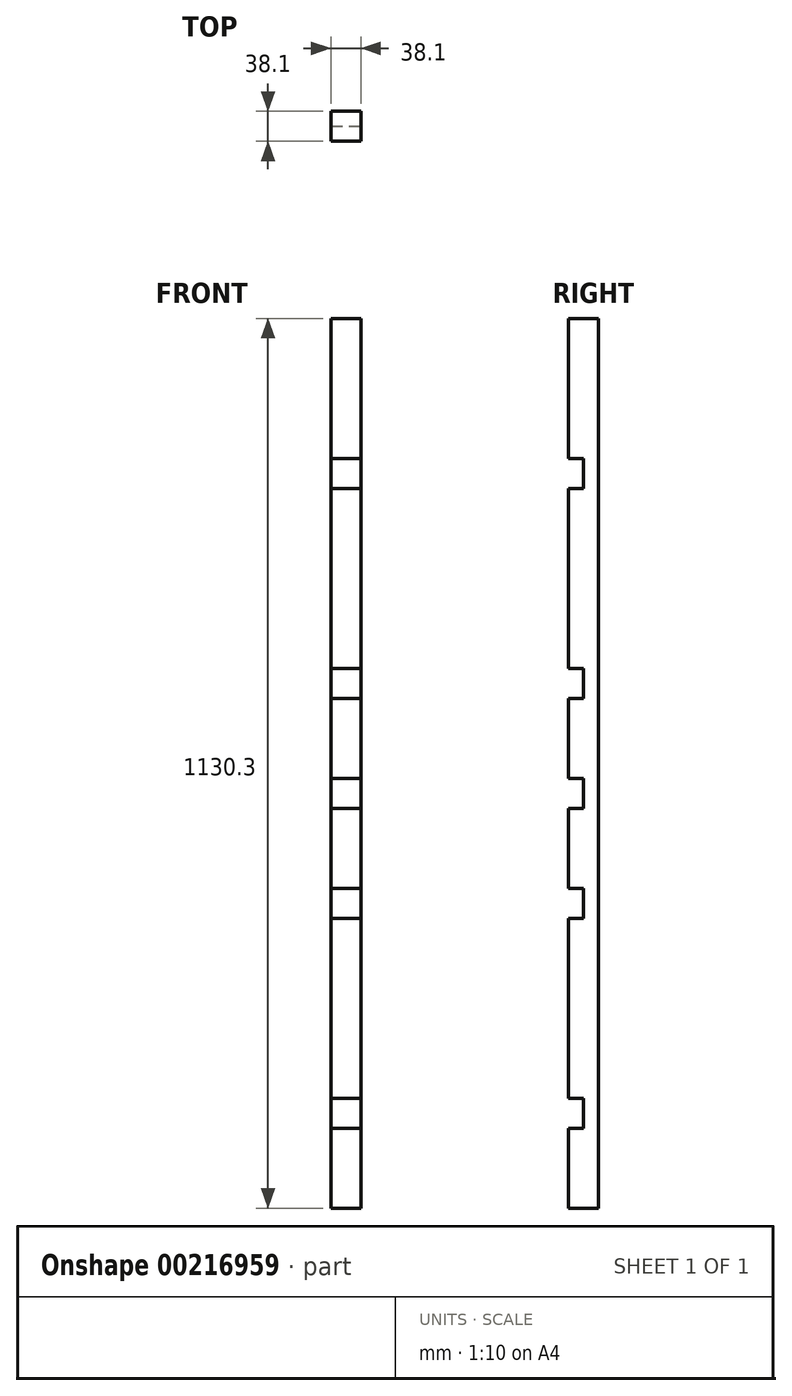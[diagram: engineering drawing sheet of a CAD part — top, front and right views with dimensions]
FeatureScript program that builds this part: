
annotation { "Feature Type Name" : "Feature", "Feature Type Description" : "" }
export const myFeature = defineFeature(function(context is Context, id is Id, definition is map)
    precondition{}
    {
        {
            var Q0;
            Q0=qCreatedBy(makeId("Top.planeOp"),FACE);
            var sketch = newSketch(context, id + "F0", { "sketchPlane" : qUnion([Q0])});
            skLineSegment(sketch, "E0", {"start": v(0, 0) * mm, "end": v(-50.8, 0) * mm});
            skLineSegment(sketch, "E1", {"start": v(0, 0) * mm, "end": v(50.8, 0) * mm});
            skLineSegment(sketch, "E2", {"start": v(50.8, 0) * mm, "end": v(50.8, 38.1) * mm});
            skLineSegment(sketch, "E3", {"start": v(88.9, 38.1) * mm, "end": v(88.9, 0) * mm});
            skLineSegment(sketch, "E4", {"start": v(88.9, 0) * mm, "end": v(317.5, 0) * mm});
            skLineSegment(sketch, "E5", {"start": v(317.5, 0) * mm, "end": v(317.5, 38.1) * mm});
            skLineSegment(sketch, "E6", {"start": v(355.6, 38.1) * mm, "end": v(355.6, 0) * mm});
            skLineSegment(sketch, "E7", {"start": v(355.6, 0) * mm, "end": v(533.4, 0) * mm});
            skLineSegment(sketch, "E8", {"start": v(533.4, 0) * mm, "end": v(533.4, 38.1) * mm});
            skLineSegment(sketch, "E9", {"start": v(-50.8, 0) * mm, "end": v(-50.8, 38.1) * mm});
            skLineSegment(sketch, "E10", {"start": v(-88.9, 38.1) * mm, "end": v(-190.5, 38.1) * mm});
            skLineSegment(sketch, "E11", {"start": v(-190.5, 38.1) * mm, "end": v(-190.5, 0) * mm});
            skLineSegment(sketch, "E12", {"start": v(-228.6, 0) * mm, "end": v(-228.6, 38.1) * mm});
            skLineSegment(sketch, "E13", {"start": v(-228.6, 38.1) * mm, "end": v(-457.2, 38.1) * mm});
            skLineSegment(sketch, "E14", {"start": v(-457.2, 38.1) * mm, "end": v(-457.2, 0) * mm});
            skLineSegment(sketch, "E15", {"start": v(-495.3, 0) * mm, "end": v(-495.3, 38.1) * mm});
            skLineSegment(sketch, "E16", {"start": v(-495.3, 38.1) * mm, "end": v(-596.9, 38.1) * mm});
            skLineSegment(sketch, "E17", {"start": v(-596.9, 38.1) * mm, "end": v(-596.9, 0) * mm});
            skLineSegment(sketch, "E18", {"start": v(-88.9, 0) * mm, "end": v(-88.9, 38.1) * mm});
            skLineSegment(sketch, "E19.trimOffspring", {"start": v(-596.9, 38.1) * mm, "end": v(-495.3, 38.1) * mm});
            skLineSegment(sketch, "E20.trimOffspring", {"start": v(-457.2, 38.1) * mm, "end": v(-228.6, 38.1) * mm});
            skLineSegment(sketch, "E21.trimOffspring", {"start": v(-190.5, 38.1) * mm, "end": v(-88.9, 38.1) * mm});
            skLineSegment(sketch, "E22.trimOffspring", {"start": v(-495.3, 0) * mm, "end": v(-596.9, 0) * mm});
            skLineSegment(sketch, "E23.trimOffspring", {"start": v(-228.6, 0) * mm, "end": v(-457.2, 0) * mm});
            skLineSegment(sketch, "E24.trimOffspring", {"start": v(-88.9, 0) * mm, "end": v(-190.5, 0) * mm});
            skLineSegment(sketch, "E25.trimOffspring", {"start": v(-50.8, 38.1) * mm, "end": v(50.8, 38.1) * mm});
            skLineSegment(sketch, "E26.trimOffspring", {"start": v(50.8, 0) * mm, "end": v(0, 0) * mm});
            skLineSegment(sketch, "E27.trimOffspring", {"start": v(88.9, 38.1) * mm, "end": v(317.5, 38.1) * mm});
            skLineSegment(sketch, "E28.trimOffspring", {"start": v(317.5, 0) * mm, "end": v(88.9, 0) * mm});
            skLineSegment(sketch, "E29.trimOffspring", {"start": v(355.6, 38.1) * mm, "end": v(533.4, 38.1) * mm});
            skLineSegment(sketch, "E30.trimOffspring", {"start": v(533.4, 0) * mm, "end": v(355.6, 0) * mm});
            skSolve(sketch);
        }
        {
            var Q0;
            Q0=qSketchRegion(id+"F0",true);
            extrude(context, id + "F1", {"entities" : qUnion([Q0]), "depth" : 19.05 * mm});
        }
        {
            var Q0;
            Q0=makeQuery(id+"F1.opExtrude","CAP_FACE",FACE,{"disambiguationData":[OSD([sQuery(id+"F0.wireOp",EDGE,"E15"),sQuery(id+"F0.wireOp",EDGE,"E17"),sQuery(id+"F0.wireOp",EDGE,"E19.trimOffspring"),sQuery(id+"F0.wireOp",EDGE,"E22.trimOffspring")])],"isStart":false});
            var sketch = newSketch(context, id + "F2", { "sketchPlane" : qUnion([Q0])});
            skLineSegment(sketch, "E31.bottom", {"start": v(-596.9, 38.1) * mm, "end": v(533.4, 38.1) * mm});
            skLineSegment(sketch, "E31.top", {"start": v(-596.9, 0) * mm, "end": v(533.4, 0) * mm});
            skLineSegment(sketch, "E31.left", {"start": v(-596.9, 38.1) * mm, "end": v(-596.9, 0) * mm});
            skLineSegment(sketch, "E31.right", {"start": v(533.4, 38.1) * mm, "end": v(533.4, 0) * mm});
            skSolve(sketch);
        }
        {
            var Q0;
            Q0=qSketchRegion(id+"F2",true);
            extrude(context, id + "F3", {"entities" : qUnion([Q0]), "depth" : 19.05 * mm});
        }
        {
            var Q0;
            Q0=makeQuery(id+"F3.opExtrude","SWEPT_BODY",BODY,{"disambiguationData":[OSD([sQuery(id+"F2.wireOp",EDGE,"E31.bottom"),sQuery(id+"F2.wireOp",EDGE,"E31.top"),sQuery(id+"F2.wireOp",EDGE,"E31.left"),sQuery(id+"F2.wireOp",EDGE,"E31.right")])]});
            var Q1;
            Q1=makeQuery(id+"F1.opExtrude","SWEPT_BODY",BODY,{"disambiguationData":[OSD([sQuery(id+"F0.wireOp",EDGE,"E2"),sQuery(id+"F0.wireOp",EDGE,"E0"),sQuery(id+"F0.wireOp",EDGE,"E9"),sQuery(id+"F0.wireOp",EDGE,"E25.trimOffspring"),sQuery(id+"F0.wireOp",EDGE,"E26.trimOffspring")])]});
            var Q2;
            Q2=makeQuery(id+"F1.opExtrude","SWEPT_BODY",BODY,{"disambiguationData":[OSD([sQuery(id+"F0.wireOp",EDGE,"E3"),sQuery(id+"F0.wireOp",EDGE,"E5"),sQuery(id+"F0.wireOp",EDGE,"E27.trimOffspring"),sQuery(id+"F0.wireOp",EDGE,"E28.trimOffspring")])]});
            var Q3;
            Q3=makeQuery(id+"F1.opExtrude","SWEPT_BODY",BODY,{"disambiguationData":[OSD([sQuery(id+"F0.wireOp",EDGE,"E6"),sQuery(id+"F0.wireOp",EDGE,"E8"),sQuery(id+"F0.wireOp",EDGE,"E29.trimOffspring"),sQuery(id+"F0.wireOp",EDGE,"E30.trimOffspring")])]});
            var Q4;
            Q4=makeQuery(id+"F1.opExtrude","SWEPT_BODY",BODY,{"disambiguationData":[OSD([sQuery(id+"F0.wireOp",EDGE,"E11"),sQuery(id+"F0.wireOp",EDGE,"E18"),sQuery(id+"F0.wireOp",EDGE,"E21.trimOffspring"),sQuery(id+"F0.wireOp",EDGE,"E24.trimOffspring")])]});
            var Q5;
            Q5=makeQuery(id+"F1.opExtrude","SWEPT_BODY",BODY,{"disambiguationData":[OSD([sQuery(id+"F0.wireOp",EDGE,"E12"),sQuery(id+"F0.wireOp",EDGE,"E14"),sQuery(id+"F0.wireOp",EDGE,"E20.trimOffspring"),sQuery(id+"F0.wireOp",EDGE,"E23.trimOffspring")])]});
            var Q6;
            Q6=makeQuery(id+"F1.opExtrude","SWEPT_BODY",BODY,{"disambiguationData":[OSD([sQuery(id+"F0.wireOp",EDGE,"E15"),sQuery(id+"F0.wireOp",EDGE,"E17"),sQuery(id+"F0.wireOp",EDGE,"E19.trimOffspring"),sQuery(id+"F0.wireOp",EDGE,"E22.trimOffspring")])]});
            booleanBodies(context, id + "F4", {"operationType" : BooleanOperationType.UNION, "tools" : qUnion([Q0, Q1, Q2, Q3, Q4, Q5, Q6])});
        }
        {
            var Q0;
            Q0=makeQuery(id+"F3.opExtrude","SWEPT_BODY",BODY,{"disambiguationData":[OSD([sQuery(id+"F2.wireOp",EDGE,"E31.bottom"),sQuery(id+"F2.wireOp",EDGE,"E31.top"),sQuery(id+"F2.wireOp",EDGE,"E31.left"),sQuery(id+"F2.wireOp",EDGE,"E31.right")])]});
            var Q1;
            Q1=makeQuery(id+"F3.opExtrude","CAP_EDGE",EDGE,{"disambiguationData":[OSD([sQuery(id+"F2.wireOp",EDGE,"E31.left")])],"isStart":false});
            transform(context, id + "F5", {"entities" : qUnion([Q0]), "transformType" : TransformType.ROTATION, "transformAxis" : qUnion([Q1]), "angle" : 90 * degree, "makeCopy" : false});
        }
        {
            var Q0;
            Q0=makeQuery(id+"F3.opExtrude","SWEPT_BODY",BODY,{"disambiguationData":[OSD([sQuery(id+"F2.wireOp",EDGE,"E31.bottom"),sQuery(id+"F2.wireOp",EDGE,"E31.top"),sQuery(id+"F2.wireOp",EDGE,"E31.left"),sQuery(id+"F2.wireOp",EDGE,"E31.right")])]});
            var Q1;
            Q1=makeQuery(id+"F3.opExtrude","CAP_EDGE",EDGE,{"disambiguationData":[OSD([sQuery(id+"F2.wireOp",EDGE,"E31.top")])],"isStart":false});
            transform(context, id + "F6", {"entities" : qUnion([Q0]), "transformType" : TransformType.ROTATION, "transformAxis" : qUnion([Q1]), "angle" : 90 * degree, "oppositeDirection" : true, "makeCopy" : false});
        }
    });
